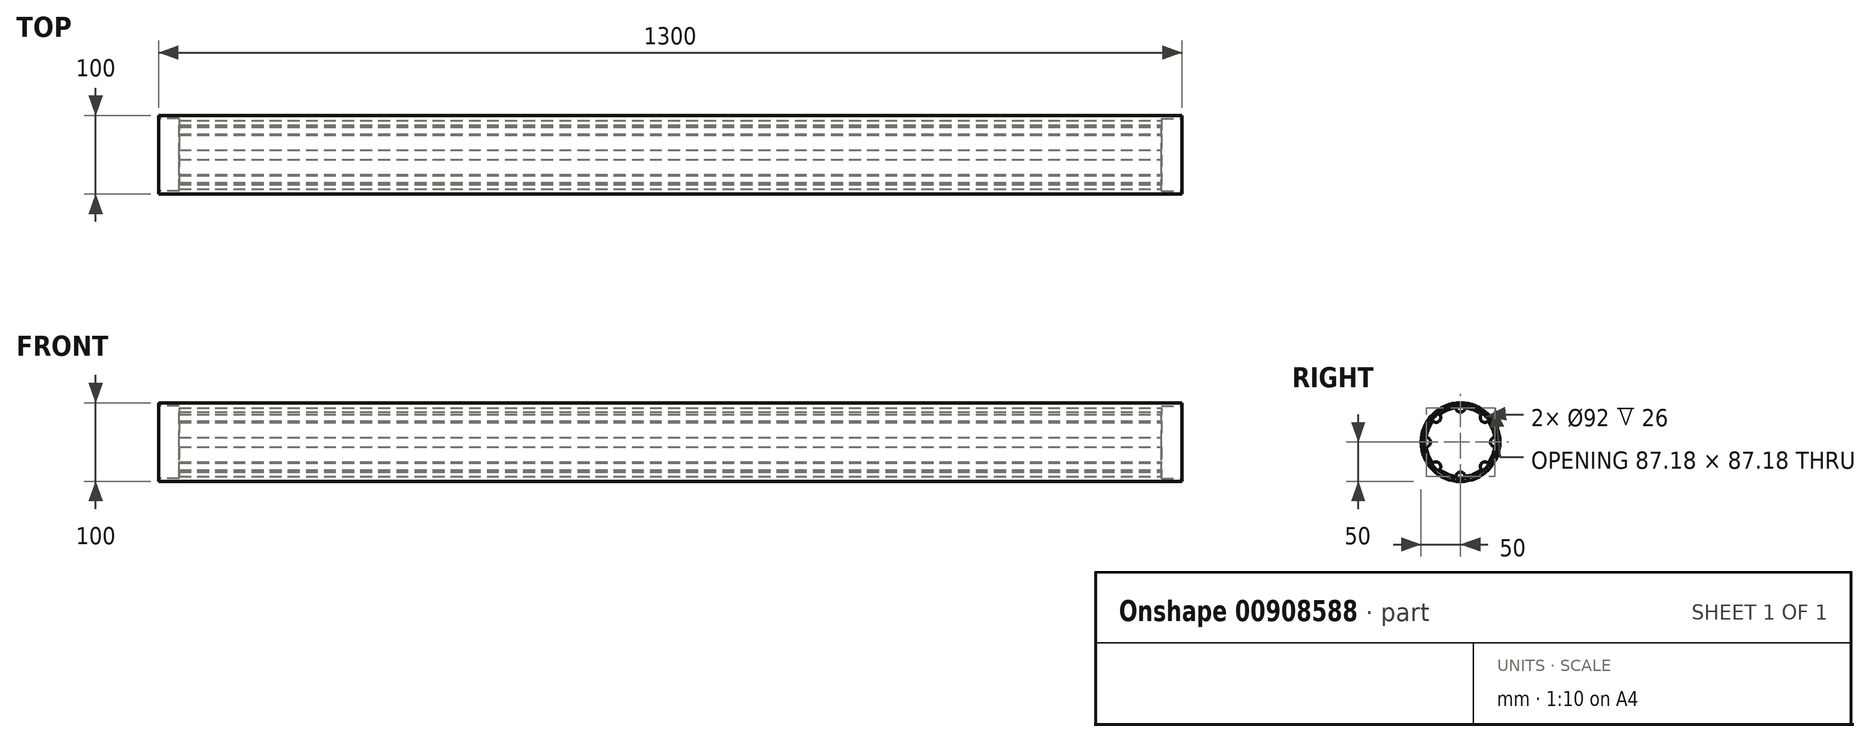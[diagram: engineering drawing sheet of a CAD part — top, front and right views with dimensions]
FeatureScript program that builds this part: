
annotation { "Feature Type Name" : "Feature", "Feature Type Description" : "" }
export const myFeature = defineFeature(function(context is Context, id is Id, definition is map)
    precondition{}
    {
        {
            var Q0;
            Q0=qCreatedBy(makeId("Right.planeOp"),FACE);
            var sketch = newSketch(context, id + "F0", { "sketchPlane" : qUnion([Q0])});
            skCircle(sketch, "E0", {"center": v(0, 0) * mm, "radius": 50 * mm});
            skArc(sketch, "E1", {"start": v(5.99, -43.6) * mm, "mid": v(16.84, -40.65) * mm, "end": v(26.6, -35.06) * mm});
            skArc(sketch, "E2", {"start": v(5.99, -43.6) * mm, "mid": v(0, -38) * mm, "end": v(-5.99, -43.6) * mm});
            skArc(sketch, "E3.1.0", {"start": v(35.06, -26.6) * mm, "mid": v(26.87, -26.87) * mm, "end": v(26.6, -35.06) * mm});
            skArc(sketch, "E3.2.0", {"start": v(43.6, 5.99) * mm, "mid": v(38, 0) * mm, "end": v(43.6, -5.99) * mm});
            skArc(sketch, "E3.3.0", {"start": v(26.6, 35.06) * mm, "mid": v(26.87, 26.87) * mm, "end": v(35.06, 26.6) * mm});
            skArc(sketch, "E3.4.0", {"start": v(-5.99, 43.6) * mm, "mid": v(0, 38) * mm, "end": v(5.99, 43.6) * mm});
            skArc(sketch, "E3.5.0", {"start": v(-35.06, 26.6) * mm, "mid": v(-26.87, 26.87) * mm, "end": v(-26.6, 35.06) * mm});
            skArc(sketch, "E3.6.0", {"start": v(-43.6, -5.99) * mm, "mid": v(-38, 0) * mm, "end": v(-43.6, 5.99) * mm});
            skArc(sketch, "E3.7.0", {"start": v(-26.6, -35.06) * mm, "mid": v(-26.87, -26.87) * mm, "end": v(-35.06, -26.6) * mm});
            skArc(sketch, "E4.trimOffspring", {"start": v(-35.06, 26.6) * mm, "mid": v(-40.65, 16.84) * mm, "end": v(-43.6, 5.99) * mm});
            skArc(sketch, "E5.trimOffspring", {"start": v(-5.99, 43.6) * mm, "mid": v(-16.84, 40.65) * mm, "end": v(-26.6, 35.06) * mm});
            skArc(sketch, "E6.trimOffspring", {"start": v(-43.6, -5.99) * mm, "mid": v(-40.65, -16.84) * mm, "end": v(-35.06, -26.6) * mm});
            skArc(sketch, "E7.trimOffspring", {"start": v(-26.6, -35.06) * mm, "mid": v(-16.84, -40.65) * mm, "end": v(-5.99, -43.6) * mm});
            skArc(sketch, "E8.trimOffspring", {"start": v(35.06, -26.6) * mm, "mid": v(40.65, -16.84) * mm, "end": v(43.6, -5.99) * mm});
            skArc(sketch, "E9.trimOffspring", {"start": v(43.6, 5.99) * mm, "mid": v(40.65, 16.84) * mm, "end": v(35.06, 26.6) * mm});
            skArc(sketch, "E10.trimOffspring", {"start": v(26.6, 35.06) * mm, "mid": v(16.84, 40.65) * mm, "end": v(5.99, 43.6) * mm});
            skSolve(sketch);
        }
        {
            var Q0;
            Q0=makeQuery(id+"F0.imprint","IMPRINT",FACE,{"disambiguationData":[TD([[makeQuery(id+"F0.imprint","IMPRINT",EDGE,{"derivedFrom":sQuery(id+"F0.wireOp",EDGE,"E0")}),1.0]])]});
            extrude(context, id + "F1", {"entities" : qUnion([Q0]), "oppositeDirection" : true, "depth" : 650 * mm, "offsetDistance" : 25 * mm});
        }
        {
            var Q0;
            Q0=qCreatedBy(makeId("Right.planeOp"),FACE);
            var sketch = newSketch(context, id + "F2", { "sketchPlane" : qUnion([Q0])});
            skCircle(sketch, "E11", {"center": v(0, 0) * mm, "radius": 46 * mm});
            skSolve(sketch);
        }
        {
            var Q0;
            Q0=makeQuery(id+"F2.imprint","IMPRINT",FACE,{"disambiguationData":[TD([[makeQuery(id+"F2.imprint","IMPRINT",EDGE,{"derivedFrom":sQuery(id+"F2.wireOp",EDGE,"E11")}),1.0]])]});
            extrude(context, id + "F3", {"entities" : qUnion([Q0]), "operationType" : NewBodyOperationType.REMOVE, "oppositeDirection" : true, "depth" : 26 * mm, "offsetDistance" : 25 * mm});
        }
        {
            var Q0;
            Q0=makeQuery(id+"F1.opExtrude","SWEPT_BODY",BODY,{"disambiguationData":[OSD([sQuery(id+"F0.wireOp",EDGE,"E0"),sQuery(id+"F0.wireOp",EDGE,"E1"),sQuery(id+"F0.wireOp",EDGE,"E2"),sQuery(id+"F0.wireOp",EDGE,"E3.1.0"),sQuery(id+"F0.wireOp",EDGE,"E3.2.0"),sQuery(id+"F0.wireOp",EDGE,"E3.3.0"),sQuery(id+"F0.wireOp",EDGE,"E3.4.0"),sQuery(id+"F0.wireOp",EDGE,"E3.5.0"),sQuery(id+"F0.wireOp",EDGE,"E3.6.0"),sQuery(id+"F0.wireOp",EDGE,"E3.7.0"),sQuery(id+"F0.wireOp",EDGE,"E4.trimOffspring"),sQuery(id+"F0.wireOp",EDGE,"E5.trimOffspring"),sQuery(id+"F0.wireOp",EDGE,"E6.trimOffspring"),sQuery(id+"F0.wireOp",EDGE,"E7.trimOffspring"),sQuery(id+"F0.wireOp",EDGE,"E8.trimOffspring"),sQuery(id+"F0.wireOp",EDGE,"E9.trimOffspring"),sQuery(id+"F0.wireOp",EDGE,"E10.trimOffspring")])]});
            var Q1;
            Q1=makeQuery(id+"F1.opExtrude","CAP_FACE",FACE,{"disambiguationData":[OSD([sQuery(id+"F0.wireOp",EDGE,"E0"),sQuery(id+"F0.wireOp",EDGE,"E1"),sQuery(id+"F0.wireOp",EDGE,"E2"),sQuery(id+"F0.wireOp",EDGE,"E3.1.0"),sQuery(id+"F0.wireOp",EDGE,"E3.2.0"),sQuery(id+"F0.wireOp",EDGE,"E3.3.0"),sQuery(id+"F0.wireOp",EDGE,"E3.4.0"),sQuery(id+"F0.wireOp",EDGE,"E3.5.0"),sQuery(id+"F0.wireOp",EDGE,"E3.6.0"),sQuery(id+"F0.wireOp",EDGE,"E3.7.0"),sQuery(id+"F0.wireOp",EDGE,"E4.trimOffspring"),sQuery(id+"F0.wireOp",EDGE,"E5.trimOffspring"),sQuery(id+"F0.wireOp",EDGE,"E6.trimOffspring"),sQuery(id+"F0.wireOp",EDGE,"E7.trimOffspring"),sQuery(id+"F0.wireOp",EDGE,"E8.trimOffspring"),sQuery(id+"F0.wireOp",EDGE,"E9.trimOffspring"),sQuery(id+"F0.wireOp",EDGE,"E10.trimOffspring")])],"isStart":false});
            mirror(context, id + "F4", {"operationType" : NewBodyOperationType.ADD, "entities" : qUnion([Q0]), "mirrorPlane" : qUnion([Q1])});
        }
    });
